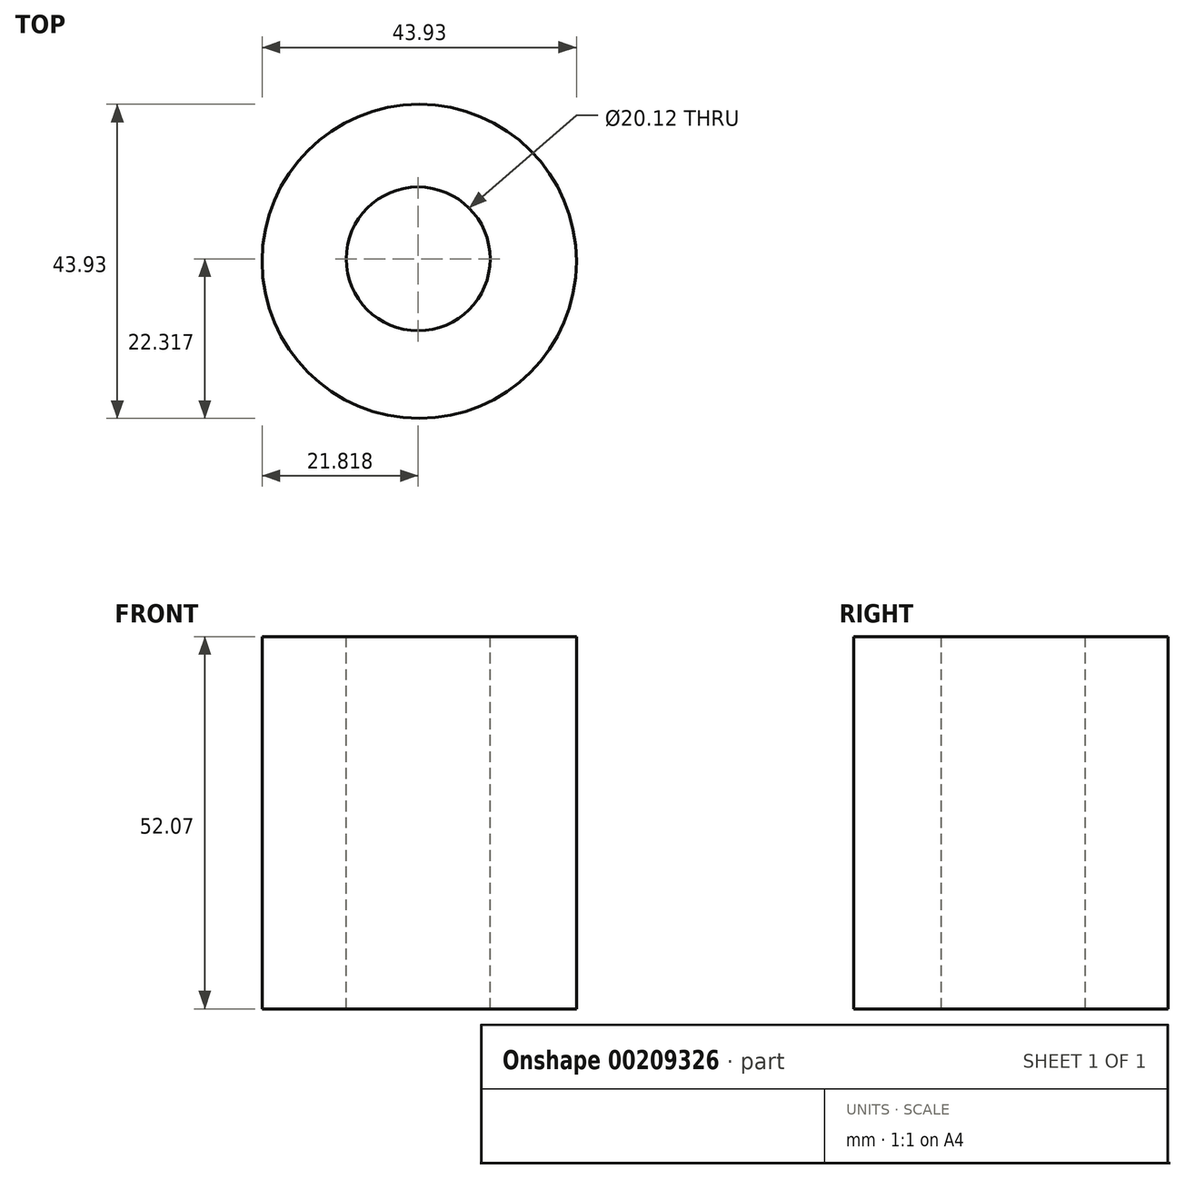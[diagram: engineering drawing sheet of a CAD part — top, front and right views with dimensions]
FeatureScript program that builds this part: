
annotation { "Feature Type Name" : "Feature", "Feature Type Description" : "" }
export const myFeature = defineFeature(function(context is Context, id is Id, definition is map)
    precondition{}
    {
        {
            var Q0;
            Q0=qCreatedBy(makeId("Top.planeOp"),FACE);
            var sketch = newSketch(context, id + "F0", { "sketchPlane" : qUnion([Q0])});
            skCircle(sketch, "E0", {"center": v(-0.43, -1.3) * mm, "radius": 21.97 * mm});
            skPoint(sketch, "E0.first.point", {"position": v(-15.45, 14.72) * mm});
            skPoint(sketch, "E0.second.point", {"position": v(15.74, -16.18) * mm});
            skPoint(sketch, "E0.third.point", {"position": v(-15.74, -17.05) * mm});
            skSolve(sketch);
        }
        {
            var Q0;
            Q0=makeQuery(id+"F0.imprint","IMPRINT",FACE,{"disambiguationData":[TD([[makeQuery(id+"F0.imprint","IMPRINT",EDGE,{"derivedFrom":sQuery(id+"F0.wireOp",EDGE,"E0")}),1.0]])]});
            extrude(context, id + "F1", {"entities" : qUnion([Q0]), "depth" : 52.07 * mm});
        }
        {
            var Q0;
            Q0=makeQuery(id+"F1.opExtrude","CAP_FACE",FACE,{"disambiguationData":[OSD([sQuery(id+"F0.wireOp",EDGE,"E0")])],"isStart":false});
            var sketch = newSketch(context, id + "F2", { "sketchPlane" : qUnion([Q0])});
            skCircle(sketch, "E1", {"center": v(-0.57, -0.95) * mm, "radius": 10.06 * mm});
            skPoint(sketch, "E1.first.point", {"position": v(-7.58, 6.27) * mm});
            skPoint(sketch, "E1.second.point", {"position": v(7.58, -6.85) * mm});
            skPoint(sketch, "E1.third.point", {"position": v(9.04, -3.93) * mm});
            skSolve(sketch);
        }
        {
            var Q0;
            Q0=makeQuery(id+"F2.imprint","IMPRINT",FACE,{"disambiguationData":[TD([[makeQuery(id+"F2.imprint","IMPRINT",EDGE,{"derivedFrom":sQuery(id+"F2.wireOp",EDGE,"E1")}),1.0]])]});
            extrude(context, id + "F3", {"entities" : qUnion([Q0]), "operationType" : NewBodyOperationType.REMOVE, "oppositeDirection" : true, "depth" : 117.1 * mm});
        }
    });
